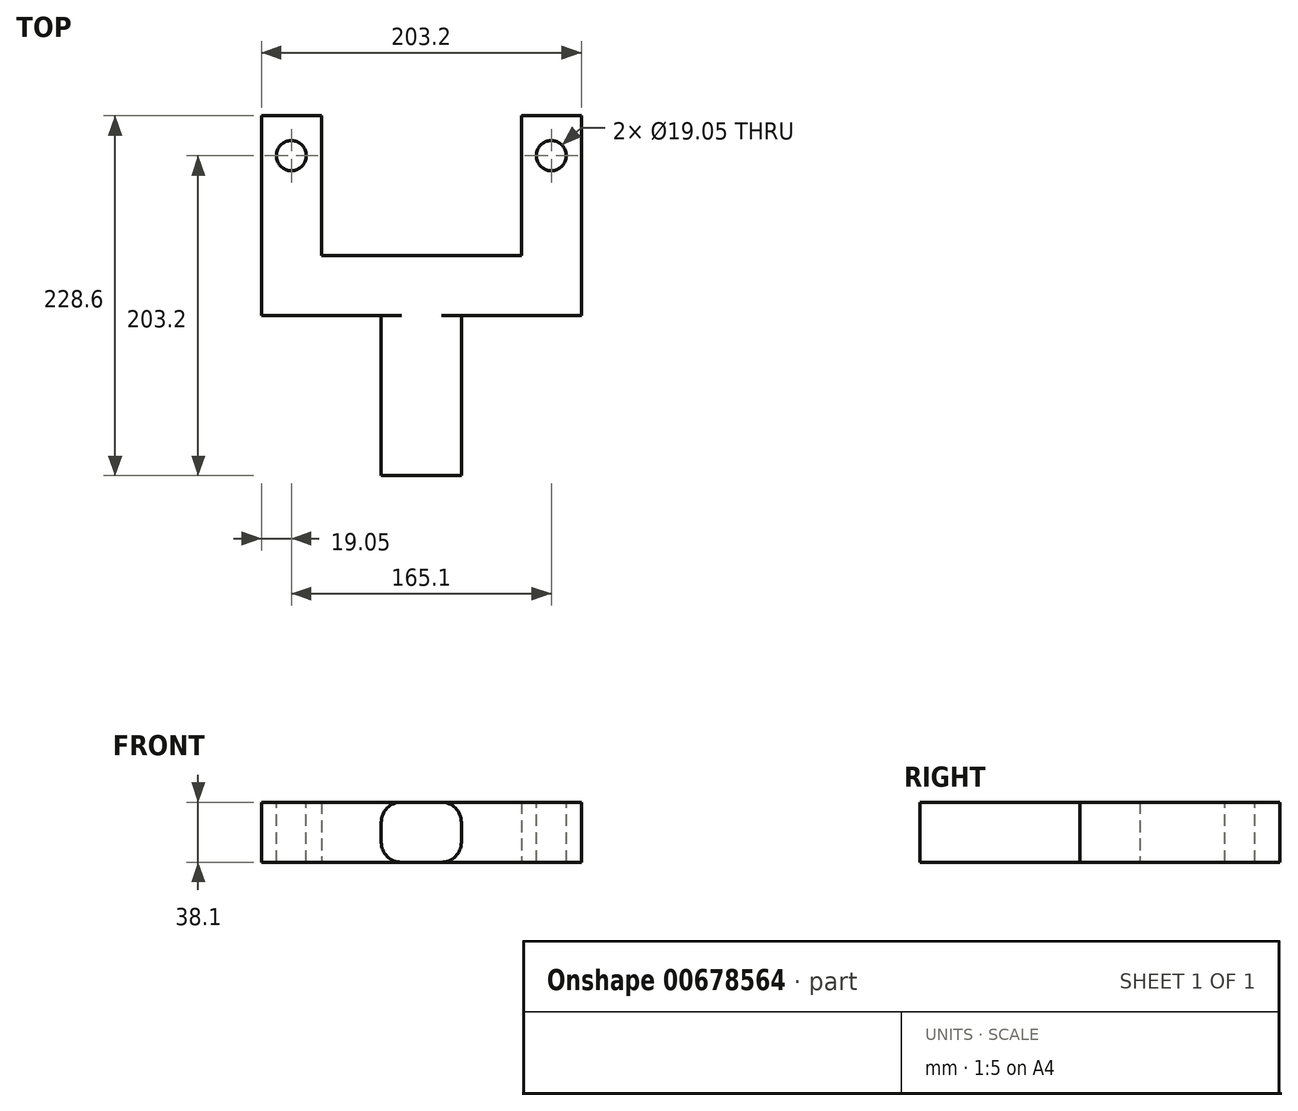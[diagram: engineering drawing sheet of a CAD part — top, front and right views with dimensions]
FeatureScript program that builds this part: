
annotation { "Feature Type Name" : "Feature", "Feature Type Description" : "" }
export const myFeature = defineFeature(function(context is Context, id is Id, definition is map)
    precondition{}
    {
        {
            var Q0;
            Q0=qCreatedBy(makeId("Top.planeOp"),FACE);
            var sketch = newSketch(context, id + "F0", { "sketchPlane" : qUnion([Q0])});
            skLineSegment(sketch, "E0.bottom", {"start": v(0, 0) * mm, "end": v(-50.8, 0) * mm});
            skLineSegment(sketch, "E0.top", {"start": v(0, 139.7) * mm, "end": v(-50.8, 139.7) * mm});
            skLineSegment(sketch, "E0.left", {"start": v(0, 0) * mm, "end": v(0, 139.7) * mm});
            skLineSegment(sketch, "E0.right", {"start": v(-50.8, 0) * mm, "end": v(-50.8, 139.7) * mm});
            skLineSegment(sketch, "E1.bottom", {"start": v(-50.8, 139.7) * mm, "end": v(-88.9, 139.7) * mm});
            skLineSegment(sketch, "E1.top", {"start": v(-50.8, 101.6) * mm, "end": v(-88.9, 101.6) * mm});
            skLineSegment(sketch, "E1.left", {"start": v(-50.8, 139.7) * mm, "end": v(-50.8, 101.6) * mm});
            skLineSegment(sketch, "E1.right", {"start": v(-88.9, 139.7) * mm, "end": v(-88.9, 101.6) * mm});
            skLineSegment(sketch, "E2.bottom", {"start": v(0, 139.7) * mm, "end": v(38.1, 139.7) * mm});
            skLineSegment(sketch, "E2.top", {"start": v(0, 101.6) * mm, "end": v(38.1, 101.6) * mm});
            skLineSegment(sketch, "E2.left", {"start": v(0, 139.7) * mm, "end": v(0, 101.6) * mm});
            skLineSegment(sketch, "E2.right", {"start": v(38.1, 139.7) * mm, "end": v(38.1, 101.6) * mm});
            skLineSegment(sketch, "E3.bottom", {"start": v(-88.9, 101.6) * mm, "end": v(-127, 101.6) * mm});
            skLineSegment(sketch, "E3.top", {"start": v(-88.9, 228.6) * mm, "end": v(-127, 228.6) * mm});
            skLineSegment(sketch, "E3.left", {"start": v(-88.9, 101.6) * mm, "end": v(-88.9, 228.6) * mm});
            skLineSegment(sketch, "E3.right", {"start": v(-127, 101.6) * mm, "end": v(-127, 228.6) * mm});
            skLineSegment(sketch, "E4.bottom", {"start": v(38.1, 101.6) * mm, "end": v(76.2, 101.6) * mm});
            skLineSegment(sketch, "E4.top", {"start": v(38.1, 228.6) * mm, "end": v(76.2, 228.6) * mm});
            skLineSegment(sketch, "E4.left", {"start": v(38.1, 101.6) * mm, "end": v(38.1, 228.6) * mm});
            skLineSegment(sketch, "E4.right", {"start": v(76.2, 101.6) * mm, "end": v(76.2, 228.6) * mm});
            skSolve(sketch);
        }
        {
            var Q0;
            Q0 = qSketchRegion(id + "F0", true);
            extrude(context, id + "F1", {"entities" : qUnion([Q0]), "depth" : 38.1 * mm, "offsetDistance" : 25.4 * mm});
        }
        {
            var Q0;
            Q0=makeQuery(id+"F1.opExtrude","CAP_EDGE",EDGE,{"disambiguationData":[OSD([sQuery(id+"F0.wireOp",EDGE,"E0.left")])],"isStart":false});
            var Q1;
            Q1=makeQuery(id+"F1.opExtrude","CAP_EDGE",EDGE,{"disambiguationData":[OSD([sQuery(id+"F0.wireOp",EDGE,"E0.right")])],"isStart":false});
            var Q2;
            Q2=makeQuery(id+"F1.opExtrude","CAP_EDGE",EDGE,{"disambiguationData":[OSD([sQuery(id+"F0.wireOp",EDGE,"E0.right")])],"isStart":true});
            var Q3;
            Q3=makeQuery(id+"F1.opExtrude","CAP_EDGE",EDGE,{"disambiguationData":[OSD([sQuery(id+"F0.wireOp",EDGE,"E0.left")])],"isStart":true});
            fillet(context, id + "F2", {"entities" : qUnion([Q0, Q1, Q2, Q3]), "radius" : 12.7 * mm, "tangentPropagation" : true, "allowEdgeOverflow" : false});
        }
        {
            var Q0;
            Q0=makeQuery(id+"F1.opExtrude","CAP_FACE",FACE,{"disambiguationData":[OSD([sQuery(id+"F0.wireOp",EDGE,"E0.bottom"),sQuery(id+"F0.wireOp",EDGE,"E0.top"),sQuery(id+"F0.wireOp",EDGE,"E0.left"),sQuery(id+"F0.wireOp",EDGE,"E0.right"),sQuery(id+"F0.wireOp",EDGE,"E1.bottom"),sQuery(id+"F0.wireOp",EDGE,"E1.top"),sQuery(id+"F0.wireOp",EDGE,"E2.bottom"),sQuery(id+"F0.wireOp",EDGE,"E2.top"),sQuery(id+"F0.wireOp",EDGE,"E3.bottom"),sQuery(id+"F0.wireOp",EDGE,"E3.top"),sQuery(id+"F0.wireOp",EDGE,"E3.left"),sQuery(id+"F0.wireOp",EDGE,"E3.right"),sQuery(id+"F0.wireOp",EDGE,"E4.bottom"),sQuery(id+"F0.wireOp",EDGE,"E4.top"),sQuery(id+"F0.wireOp",EDGE,"E4.left"),sQuery(id+"F0.wireOp",EDGE,"E4.right")])],"isStart":false});
            var sketch = newSketch(context, id + "F3", { "sketchPlane" : qUnion([Q0])});
            skLineSegment(sketch, "E5", {"start": v(-127, 203.2) * mm, "end": v(-88.9, 203.2) * mm});
            skLineSegment(sketch, "E6", {"start": v(38.1, 203.2) * mm, "end": v(76.2, 203.2) * mm});
            skCircle(sketch, "E7", {"center": v(-107.95, 203.2) * mm, "radius": 9.53 * mm});
            skCircle(sketch, "E8", {"center": v(57.15, 203.2) * mm, "radius": 9.53 * mm});
            skPoint(sketch, "E9", {"position": v(-107.95, 228.6) * mm});
            skSolve(sketch);
        }
        {
            var Q0;
            {var subQ0=sQuery(id+"F3.wireOp",EDGE,"E7");var subQ1=sQuery(id+"F3.wireOp",EDGE,"E5");var subQ2=makeQuery(id+"F3.imprint","INTERSECT",VERTEX,{"disambiguationData":[OD(0.0)],"derivedFrom":[subQ1,subQ0]});Q0=makeQuery(id+"F3.imprint","IMPRINT",FACE,{"disambiguationData":[TD([[makeQuery(id+"F3.imprint","IMPRINT",EDGE,{"disambiguationData":[TD([[subQ2,-1.0]])],"derivedFrom":subQ1}),-1.0]])]});}
            var Q1;
            {var subQ0=sQuery(id+"F3.wireOp",EDGE,"E8");var subQ1=sQuery(id+"F3.wireOp",EDGE,"E6");var subQ2=makeQuery(id+"F3.imprint","INTERSECT",VERTEX,{"disambiguationData":[OD(0.0)],"derivedFrom":[subQ1,subQ0]});Q1=makeQuery(id+"F3.imprint","IMPRINT",FACE,{"disambiguationData":[TD([[makeQuery(id+"F3.imprint","IMPRINT",EDGE,{"disambiguationData":[TD([[subQ2,-1.0]])],"derivedFrom":subQ1}),-1.0]])]});}
            var Q2;
            {var subQ0=sQuery(id+"F3.wireOp",EDGE,"E8");var subQ1=sQuery(id+"F3.wireOp",EDGE,"E6");var subQ2=makeQuery(id+"F3.imprint","INTERSECT",VERTEX,{"disambiguationData":[OD(0.0)],"derivedFrom":[subQ1,subQ0]});Q2=makeQuery(id+"F3.imprint","IMPRINT",FACE,{"disambiguationData":[TD([[makeQuery(id+"F3.imprint","IMPRINT",EDGE,{"disambiguationData":[TD([[subQ2,-1.0]])],"derivedFrom":subQ1}),1.0]])]});}
            var Q3;
            {var subQ0=sQuery(id+"F3.wireOp",EDGE,"E7");var subQ1=sQuery(id+"F3.wireOp",EDGE,"E5");var subQ2=makeQuery(id+"F3.imprint","INTERSECT",VERTEX,{"disambiguationData":[OD(0.0)],"derivedFrom":[subQ1,subQ0]});Q3=makeQuery(id+"F3.imprint","IMPRINT",FACE,{"disambiguationData":[TD([[makeQuery(id+"F3.imprint","IMPRINT",EDGE,{"disambiguationData":[TD([[subQ2,-1.0]])],"derivedFrom":subQ1}),1.0]])]});}
            extrude(context, id + "F4", {"entities" : qUnion([Q0, Q1, Q2, Q3]), "operationType" : NewBodyOperationType.REMOVE, "endBound" : BoundingType.THROUGH_ALL, "oppositeDirection" : true, "depth" : 63.5 * mm, "offsetDistance" : 25.4 * mm});
        }
    });
